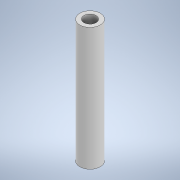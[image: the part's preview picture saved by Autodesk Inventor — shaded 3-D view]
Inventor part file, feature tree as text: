
AUTODESK INVENTOR PART (.ipt)
format: ipt  version: 2021 (Build 250183000, 183)  size: 94,208 bytes
history: native  units: mm
features: extrude x1, sketch x1
ambient origin geometry x8: Origin, YZ Plane, XZ Plane, XY Plane, X Axis, Y Axis, Z Axis, Center Point
bodies: Solid1 (feature_tree)
feature tree (2):
  extrude  "Extrusion1"  Depth=30.0mm
  sketch  "Sketch1"  dims[d0=3.0mm d1=5.0mm d2=30.0mm d3=0.0mm]
